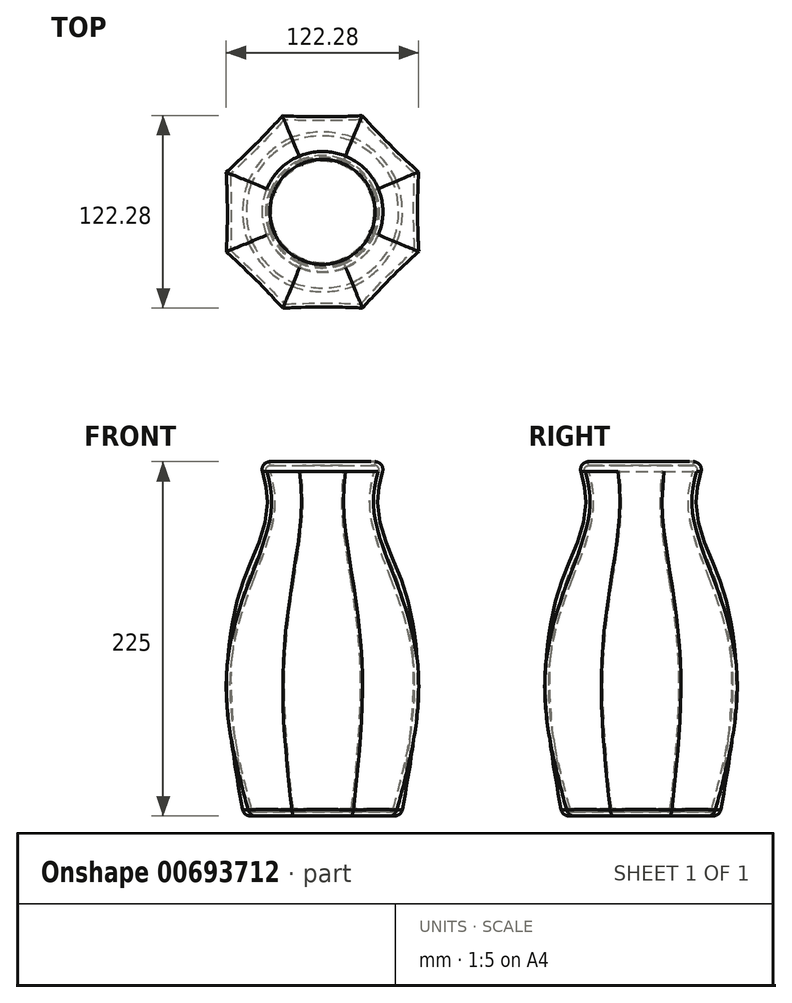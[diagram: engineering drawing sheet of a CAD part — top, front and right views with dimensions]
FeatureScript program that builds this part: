
annotation { "Feature Type Name" : "Feature", "Feature Type Description" : "" }
export const myFeature = defineFeature(function(context is Context, id is Id, definition is map)
    precondition{}
    {
        {
            var Q0;
            Q0=qCreatedBy(makeId("Top.planeOp"),FACE);
            var sketch = newSketch(context, id + "F0", { "sketchPlane" : qUnion([Q0])});
            skCircle(sketch, "E0", {"center": v(0, 0) * mm, "radius": 50 * mm});
            skSolve(sketch);
        }
        {
            var Q0;
            Q0=qCreatedBy(makeId("Top.planeOp"),FACE);
            cPlane(context, id + "F1", {"entities" : qUnion([Q0]), "cplaneType" : CPlaneType.OFFSET, "offset" : 100 * mm, "width" : 150 * mm, "height" : 150 * mm});
        }
        {
            var Q0;
            Q0=qCreatedBy(id+"F1.planeOp",FACE);
            var sketch = newSketch(context, id + "F2", { "sketchPlane" : qUnion([Q0])});
            skCircle(sketch, "E1.cCircle", {"center": v(0, 0) * mm, "radius": 60 * mm, "construction": true});
            skLineSegment(sketch, "E1.0", {"start": v(24.74, 60.05) * mm, "end": v(59.95, 24.97) * mm});
            skLineSegment(sketch, "E1.1", {"start": v(59.95, 24.97) * mm, "end": v(60.05, -24.74) * mm});
            skLineSegment(sketch, "E1.2", {"start": v(60.05, -24.74) * mm, "end": v(24.97, -59.95) * mm});
            skLineSegment(sketch, "E1.3", {"start": v(24.97, -59.95) * mm, "end": v(-24.74, -60.05) * mm});
            skLineSegment(sketch, "E1.4", {"start": v(-24.74, -60.05) * mm, "end": v(-59.95, -24.97) * mm});
            skLineSegment(sketch, "E1.5", {"start": v(-59.95, -24.97) * mm, "end": v(-60.05, 24.74) * mm});
            skLineSegment(sketch, "E1.6", {"start": v(-60.05, 24.74) * mm, "end": v(-24.97, 59.95) * mm});
            skLineSegment(sketch, "E1.7", {"start": v(-24.97, 59.95) * mm, "end": v(24.74, 60.05) * mm});
            skPoint(sketch, "E1.0.midPoint", {"position": v(42.35, 42.5) * mm});
            skSolve(sketch);
        }
        {
            var Q0;
            Q0=qCreatedBy(id+"F1.planeOp",FACE);
            cPlane(context, id + "F3", {"entities" : qUnion([Q0]), "cplaneType" : CPlaneType.OFFSET, "offset" : 50 * mm, "width" : 150 * mm, "height" : 150 * mm});
        }
        {
            var Q0;
            Q0=qCreatedBy(id+"F3.planeOp",FACE);
            var sketch = newSketch(context, id + "F4", { "sketchPlane" : qUnion([Q0])});
            skCircle(sketch, "E2", {"center": v(0, 0) * mm, "radius": 50 * mm});
            skSolve(sketch);
        }
        {
            var Q0;
            Q0=qCreatedBy(id+"F3.planeOp",FACE);
            cPlane(context, id + "F5", {"entities" : qUnion([Q0]), "cplaneType" : CPlaneType.OFFSET, "offset" : 25 * mm, "width" : 150 * mm, "height" : 150 * mm});
        }
        {
            var Q0;
            Q0=qCreatedBy(id+"F5.planeOp",FACE);
            var sketch = newSketch(context, id + "F6", { "sketchPlane" : qUnion([Q0])});
            skCircle(sketch, "E3", {"center": v(0, 0) * mm, "radius": 40 * mm});
            skSolve(sketch);
        }
        {
            var Q0;
            Q0=qCreatedBy(id+"F5.planeOp",FACE);
            cPlane(context, id + "F7", {"entities" : qUnion([Q0]), "cplaneType" : CPlaneType.OFFSET, "offset" : 25 * mm, "width" : 150 * mm, "height" : 150 * mm});
        }
        {
            var Q0;
            Q0=qCreatedBy(id+"F7.planeOp",FACE);
            var sketch = newSketch(context, id + "F8", { "sketchPlane" : qUnion([Q0])});
            skCircle(sketch, "E4", {"center": v(0, 0) * mm, "radius": 35 * mm});
            skSolve(sketch);
        }
        {
            var Q0;
            Q0=qCreatedBy(id+"F7.planeOp",FACE);
            cPlane(context, id + "F9", {"entities" : qUnion([Q0]), "cplaneType" : CPlaneType.OFFSET, "offset" : 25 * mm, "width" : 150 * mm, "height" : 150 * mm});
        }
        {
            var Q0;
            Q0=qCreatedBy(id+"F9.planeOp",FACE);
            var sketch = newSketch(context, id + "F10", { "sketchPlane" : qUnion([Q0])});
            skCircle(sketch, "E5", {"center": v(0, 0) * mm, "radius": 40 * mm});
            skSolve(sketch);
        }
        {
            var Q0;
            Q0=makeQuery(id+"F0.imprint","IMPRINT",FACE,{"disambiguationData":[TD([[makeQuery(id+"F0.imprint","IMPRINT",EDGE,{"derivedFrom":sQuery(id+"F0.wireOp",EDGE,"E0")}),1.0]])]});
            var Q1;
            Q1=makeQuery(id+"F2.imprint","IMPRINT",FACE,{"disambiguationData":[TD([[makeQuery(id+"F2.imprint","IMPRINT",EDGE,{"derivedFrom":sQuery(id+"F2.wireOp",EDGE,"E1.0")}),-1.0]])]});
            var Q2;
            Q2=makeQuery(id+"F4.imprint","IMPRINT",FACE,{"disambiguationData":[TD([[makeQuery(id+"F4.imprint","IMPRINT",EDGE,{"derivedFrom":sQuery(id+"F4.wireOp",EDGE,"E2")}),1.0]])]});
            var Q3;
            Q3=makeQuery(id+"F6.imprint","IMPRINT",FACE,{"disambiguationData":[TD([[makeQuery(id+"F6.imprint","IMPRINT",EDGE,{"derivedFrom":sQuery(id+"F6.wireOp",EDGE,"E3")}),1.0]])]});
            var Q4;
            Q4=makeQuery(id+"F8.imprint","IMPRINT",FACE,{"disambiguationData":[TD([[makeQuery(id+"F8.imprint","IMPRINT",EDGE,{"derivedFrom":sQuery(id+"F8.wireOp",EDGE,"E4")}),1.0]])]});
            var Q5;
            Q5=makeQuery(id+"F10.imprint","IMPRINT",FACE,{"disambiguationData":[TD([[makeQuery(id+"F10.imprint","IMPRINT",EDGE,{"derivedFrom":sQuery(id+"F10.wireOp",EDGE,"E5")}),1.0]])]});
            loft(context, id + "F11", {"sheetProfilesArray" : [{ "sheetProfileEntities" : qUnion([Q0]) }, { "sheetProfileEntities" : qUnion([Q1]) }, { "sheetProfileEntities" : qUnion([Q2]) }, { "sheetProfileEntities" : qUnion([Q3]) }, { "sheetProfileEntities" : qUnion([Q4]) }, { "sheetProfileEntities" : qUnion([Q5]) }]});
        }
        {
            var Q0;
            Q0=makeQuery(id+"F11.opLoft","CAP_FACE",FACE,{"disambiguationData":[OSD([makeQuery(id+"F0.imprint","IMPRINT",FACE,{"disambiguationData":[TD([[makeQuery(id+"F0.imprint","IMPRINT",EDGE,{"derivedFrom":sQuery(id+"F0.wireOp",EDGE,"E0")}),1.0]])]})])],"isStart":true});
            var Q1;
            Q1=makeQuery(id+"F11.opLoft","CAP_FACE",FACE,{"disambiguationData":[OSD([makeQuery(id+"F10.imprint","IMPRINT",FACE,{"disambiguationData":[TD([[makeQuery(id+"F10.imprint","IMPRINT",EDGE,{"derivedFrom":sQuery(id+"F10.wireOp",EDGE,"E5")}),1.0]])]})])],"isStart":true});
            fillet(context, id + "F12", {"entities" : qUnion([Q0, Q1]), "radius" : 5 * mm, "tangentPropagation" : true, "allowEdgeOverflow" : false});
        }
        {
            var Q0;
            Q0=makeQuery(id+"F11.opLoft","CAP_FACE",FACE,{"disambiguationData":[OSD([makeQuery(id+"F10.imprint","IMPRINT",FACE,{"disambiguationData":[TD([[makeQuery(id+"F10.imprint","IMPRINT",EDGE,{"derivedFrom":sQuery(id+"F10.wireOp",EDGE,"E5")}),1.0]])]})])],"isStart":true});
            shell(context, id + "F13", {"entities" : qUnion([Q0]), "thickness" : 2.5 * mm});
        }
    });
